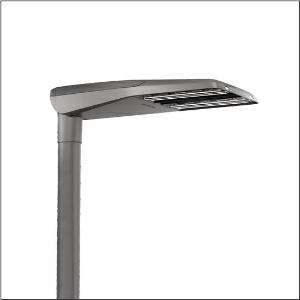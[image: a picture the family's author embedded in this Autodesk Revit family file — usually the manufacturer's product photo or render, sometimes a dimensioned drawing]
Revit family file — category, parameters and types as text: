
# Revit family: streetlight_sl_11_iq_midi___st1_0ab_5xc3n51f08le_f358
name_source: partatom
category: Lighting Fixtures
units: mm (PartAtom-declared; Revit-internal decimal feet)

## family parameters
Cut with Voids When Loaded = No
Host = Face
Light Source = No
Part Type = Normal
Room Calculation Point = No
Round Connector Dimension = Use Diameter
Shared = No

## types (1)
- --- (1 x LED, 7760 lm, 60.4 W, 3000K)
    Apparent Load = 60 VA
    CIE Flux Codes = 29 63 95 100 100
    Color Rendering = 70
    Color Temperature = 3000K
    Default Elevation = 1800 mm
    Description = Streetlight SL 11 iQ midi, mast luminaire, primary light control with 3 zone facetted reflector, of plastic, silver coated, highly specular, primary optical cover: cover, of PMMA, transparent, light distribution: ST1.0aB, light emission: direct distribution, primary light characteristic: asymmetric, installation type: post-top, side-entry, LED, High Power LED, rated luminous flux: 7.760lm, luminous efficacy: 129lm/W, light colour: 730, colour temperature: 3000K, control: optimised constant luminous flux control (CLO 2.0), Street-Remote, Desk-Remote (wireless, voltage-free reading and setting of iQ features in the workshop via application-optimized NFC function/RFID function), Light-Fading, Smart-Wire, Night-Set, Lumen-Switch, Temp-Guard, Auto-Match, with cable H07RN-F 5x 1.5mm², mains connection: 230..240V, AC, 50/60Hz, connection cable pre-assembled, cable length: 8,5m, start of lifetime: 60W, end of service life: 63W, reduction: 30W, luminaire housing, of diecast aluminium, powder-coated, Siteco® metallic grey (DB 702S), please order mast flange separately, inclination adjustable without tools: 0°, 5°, 10°, 15° (post-top) | 0°, -5°, -10°, -15° (side-entry), sealing non-destructively replaceable, multi-level sealing system, length: 780mm, width: 376mm, height: 118mm, mast flange for spigot size: 42mm (side-entry): 5XC10008XM4, 60/48mm (side-entry/post-top): 5XC10108XM2, 76/60mm (side-entry/post-top): 5XC10108XM1, equipment: standard, protection rating (complete): IP66, insulation class (complete): insulation class II (safety insulation), certification: CE, ENEC, VDE, impact resistance: IK09, permissible operating ambient temperature for outdoor applications: -25..+50°C, standard-compliant lighting for roads and squares, Environmental Product Declaration (EPD) tested and certified by an independent institute, packaging unit: 1 piece

Light Distribution: ST1.0aB
    Height = 118 mm
    Lamp = 1 x LED
    Lamp Light Flux = 7760 lm
    Lamp Power = 60.4 W
    Lamp count = 1
    Length = 780 mm
    Luminous efficacy = 128 lm/W
    Manufacturer = Siteco
    ModVariant = No
    Model = 5XC3N51F08LE
    Number of Poles = 1
    OnlyDefault = Yes
    Power Factor = 1
    Product Name = Streetlight SL 11 iQ midi | ST1.0aB
    Product group = mast luminaire | pylon top
    ProductGroupID = 6100
    Protection Class = Protection class II
    Protection Degree = IP 66
    RLX_Detail_Level = 1
    RLX_Emergency_Light_Flux = 0 lm
    RLX_Emergency_Type = 0
    RLX_Emergency_Type_DB = No
    RlxData = <blob elided: 70089 chars, md5=05c94ab0>
    Socket = socket
    Standby Power = 0 W
    System Light Flux = 7760 lm
    System Power = 60 W
    Type Comments = factory setting: luminous flux: 100 % | dim-lin: 254 | 520 mA
    Type Image = l_1005960.jpg
    URL = http://relux.com
    VarID = @adj_020183
    Voltage = 0 V
    Weight = 0.00 kg
    Width = 376 mm

## geometry (parser evidence)
native form markers: Blend x4, Sweep x11
no freeform markers — native parametric forms only
